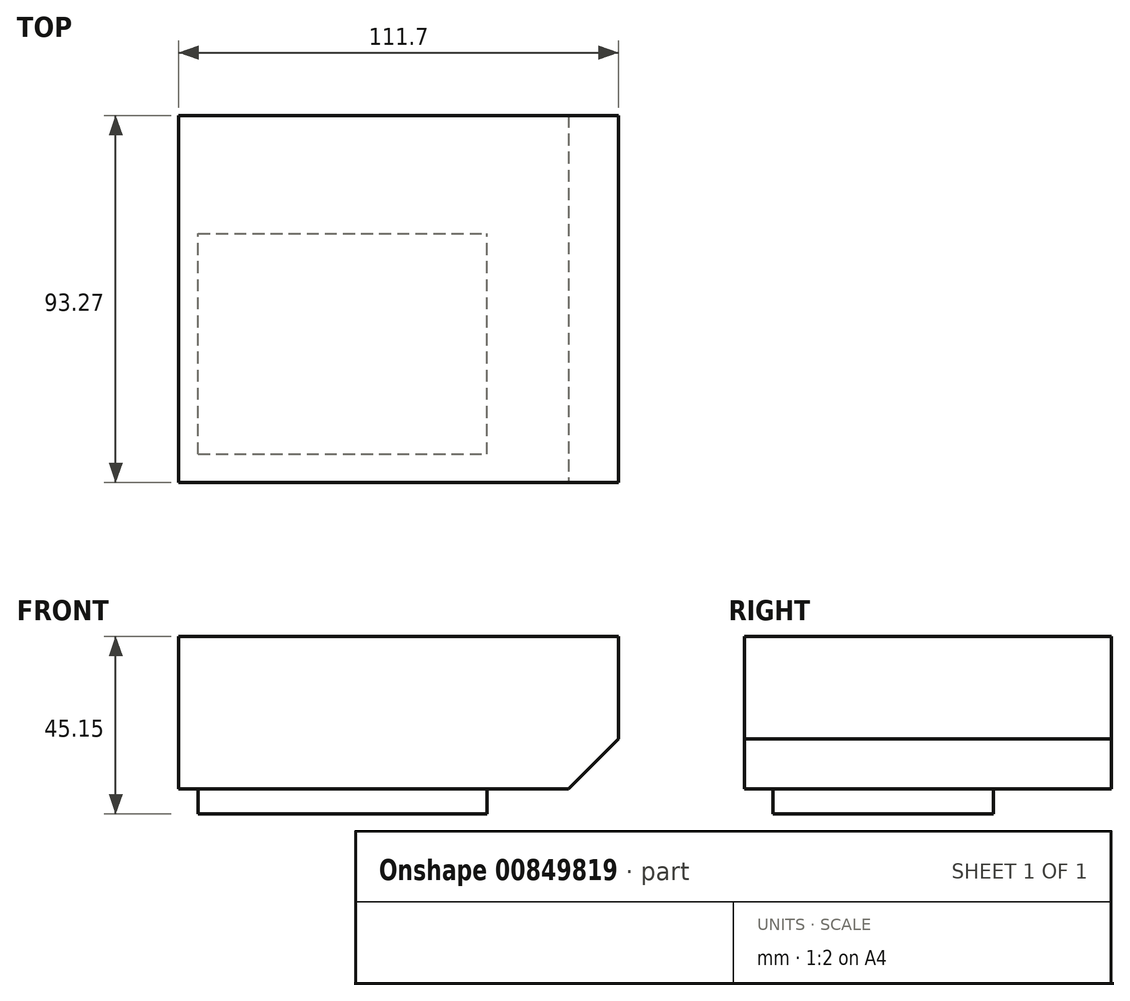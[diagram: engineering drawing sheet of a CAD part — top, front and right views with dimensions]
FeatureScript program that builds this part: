
annotation { "Feature Type Name" : "Feature", "Feature Type Description" : "" }
export const myFeature = defineFeature(function(context is Context, id is Id, definition is map)
    precondition{}
    {
        {
            var Q0;
            Q0=qCreatedBy(makeId("Top.planeOp"),FACE);
            var sketch = newSketch(context, id + "F0", { "sketchPlane" : qUnion([Q0])});
            skLineSegment(sketch, "E0.bottom", {"start": v(-43, 0) * mm, "end": v(68.69, 0) * mm});
            skLineSegment(sketch, "E0.top", {"start": v(-43, 93.27) * mm, "end": v(68.69, 93.27) * mm});
            skLineSegment(sketch, "E0.left", {"start": v(-43, 0) * mm, "end": v(-43, 93.27) * mm});
            skLineSegment(sketch, "E0.right", {"start": v(68.69, 0) * mm, "end": v(68.69, 93.27) * mm});
            skSolve(sketch);
        }
        {
            var Q0;
            Q0 = qSketchRegion(id + "F0", true);
            extrude(context, id + "F1", {"entities" : qUnion([Q0]), "oppositeDirection" : true, "depth" : 38.75 * mm, "offsetDistance" : 25.4 * mm});
        }
        {
            var Q0;
            Q0=makeQuery(id+"F1.opExtrude","CAP_EDGE",EDGE,{"disambiguationData":[OSD([sQuery(id+"F0.wireOp",EDGE,"E0.right")])],"isStart":false});
            chamfer(context, id + "F2", {"entities" : qUnion([Q0]), "width" : 12.7 * mm, "tangentPropagation" : true});
        }
        {
            var Q0;
            Q0=makeQuery(id+"F1.opExtrude","CAP_FACE",FACE,{"disambiguationData":[OSD([sQuery(id+"F0.wireOp",EDGE,"E0.bottom"),sQuery(id+"F0.wireOp",EDGE,"E0.top"),sQuery(id+"F0.wireOp",EDGE,"E0.left"),sQuery(id+"F0.wireOp",EDGE,"E0.right")])],"isStart":false});
            var sketch = newSketch(context, id + "F3", { "sketchPlane" : qUnion([Q0])});
            skLineSegment(sketch, "E1.bottom", {"start": v(-38.07, -7.27) * mm, "end": v(35.27, -7.27) * mm});
            skLineSegment(sketch, "E1.top", {"start": v(-38.07, -63.27) * mm, "end": v(35.27, -63.27) * mm});
            skLineSegment(sketch, "E1.left", {"start": v(-38.07, -7.27) * mm, "end": v(-38.07, -63.27) * mm});
            skLineSegment(sketch, "E1.right", {"start": v(35.27, -7.27) * mm, "end": v(35.27, -63.27) * mm});
            skSolve(sketch);
        }
        {
            var Q0;
            Q0=makeQuery(id+"F3.imprint","IMPRINT",FACE,{"disambiguationData":[TD([[makeQuery(id+"F3.imprint","IMPRINT",EDGE,{"derivedFrom":sQuery(id+"F3.wireOp",EDGE,"E1.bottom")}),-1.0]])]});
            extrude(context, id + "F4", {"entities" : qUnion([Q0]), "operationType" : NewBodyOperationType.ADD, "depth" : 6.4 * mm, "offsetDistance" : 25.4 * mm});
        }
    });
